# Revit family: DSA
name_source: partatom
category: Air Terminals
revit_build: Autodesk Revit MEP 2012 (Build: 20110309_2315(x64)
units: mm (PartAtom-declared; Revit-internal decimal feet)

## types (5) — shared parameters
Manufacturer = INNES
Material = Aluminio
Máxima velocidad de chorro = 4000 FPM
Mínima presión estática = 0.04 in-wg
Mínima velocidad de chorro = 750 FPM
URL = http://www.innes.com
ancho banda A = 2"
ancho banda b = 1/4"

## per-type parameters (varying)
| type | B | C | D | Duct | E | G | Max Flow | Min Flow | Máxima presión estática | Máximo nivel de ruido (NC) | b | c | c ext | g |
| DSA-08 | 9 13/16" | 7 31/32" | 1 3/4" | 4 19/64" | 5 15/32" | 3 1/32" | 340 CFM | 60 CFM | 1.20 in-wg | 40 | 4 29/32" | 3 63/64" | 4 3/64" | 1 33/64" |
| DSA-10 | 12 23/32" | 10 19/32" | 2 1/16" | 5 39/64" | 7 5/8" | 4 9/16" | 660 CFM | 120 CFM | 1.20 in-wg | 39 | 6 23/64" | 5 19/64" | 5 23/64" | 2 9/32" |
| DSA-12 | 14 3/16" | 12 1/16" | 2 7/16" | 6 11/32" | 8 11/16" | 5 9/32" | 920 CFM | 170 CFM | 1.20 in-wg | 40 | 7 3/32" | 6 1/32" | 6 3/32" | 2 41/64" |
| DSA-16 | 18 3/4" | 16 1/4" | 4 11/32" | 8 7/16" | 10 3/4" | 7 9/32" | 1790 CFM | 340 CFM | 1.19 in-wg | 45 | 9 3/8" | 8 1/8" | 8 3/16" | 3 41/64" |
| DSA-20 | 21 1/16" | 18 19/32" | 3 13/16" | 9 39/64" | 12 9/16" | 10 9/32" | 3260 CFM | 610 CFM | 1.20 in-wg | 46 | 10 17/32" | 9 19/64" | 9 23/64" | 5 9/64" |

## geometry (parser evidence)
native form markers: Sweep x1
no freeform markers — native parametric forms only
